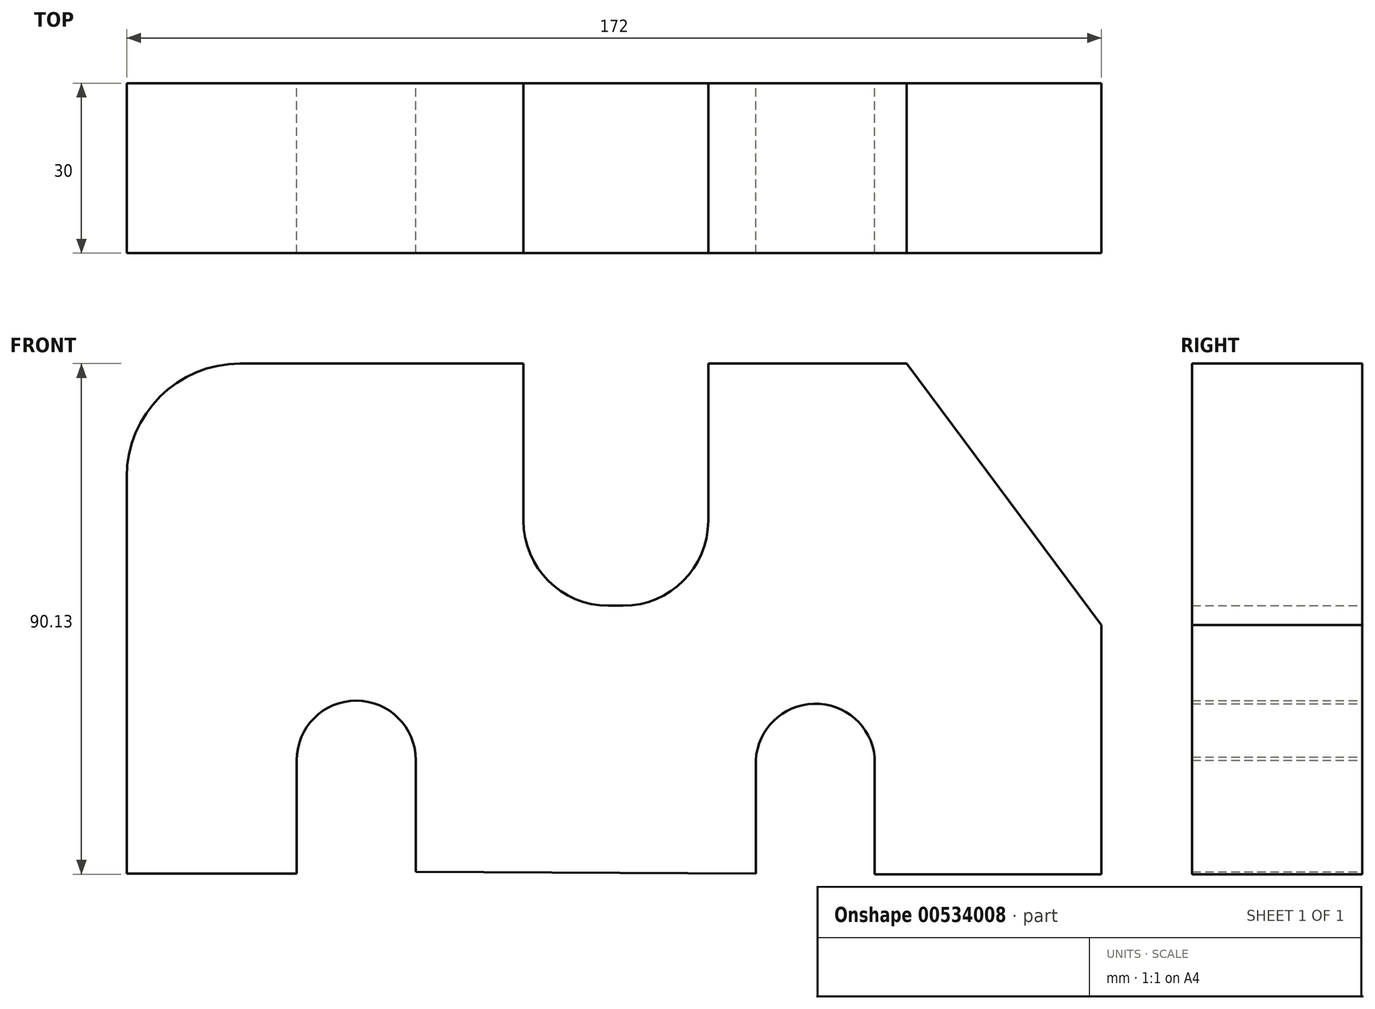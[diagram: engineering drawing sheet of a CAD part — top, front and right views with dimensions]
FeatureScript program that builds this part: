
annotation { "Feature Type Name" : "Feature", "Feature Type Description" : "" }
export const myFeature = defineFeature(function(context is Context, id is Id, definition is map)
    precondition{}
    {
        {
            var Q0;
            Q0=qCreatedBy(makeId("Front.planeOp"),FACE);
            var sketch = newSketch(context, id + "F0", { "sketchPlane" : qUnion([Q0])});
            skLineSegment(sketch, "E0", {"start": v(-52.5, -20.13) * mm, "end": v(-52.5, -40.13) * mm});
            skLineSegment(sketch, "E1", {"start": v(-52.5, -40.13) * mm, "end": v(-82.5, -40.13) * mm});
            skLineSegment(sketch, "E2", {"start": v(-82.5, -40.13) * mm, "end": v(-82.5, 29.87) * mm});
            skLineSegment(sketch, "E3", {"start": v(-62.5, 49.87) * mm, "end": v(-12.5, 49.87) * mm});
            skLineSegment(sketch, "E4", {"start": v(-12.5, 49.87) * mm, "end": v(-12.5, 22.12) * mm});
            skLineSegment(sketch, "E5", {"start": v(2.5, 7.12) * mm, "end": v(5.1, 7.12) * mm});
            skLineSegment(sketch, "E6", {"start": v(20.1, 22.12) * mm, "end": v(20.1, 49.87) * mm});
            skPoint(sketch, "E7.visualSharp", {"position": v(-82.5, 49.87) * mm});
            skArc(sketch, "E7.filletArc", {"start": v(-62.5, 49.87) * mm, "mid": v(-76.64, 44.02) * mm, "end": v(-82.5, 29.87) * mm});
            skPoint(sketch, "E8.start.orphan", {"position": v(64.04, -10.18) * mm});
            skLineSegment(sketch, "E9", {"start": v(28.5, -20.13) * mm, "end": v(28.5, -40.13) * mm});
            skPoint(sketch, "E10.start.orphan", {"position": v(-31.5, -10.18) * mm});
            skLineSegment(sketch, "E11", {"start": v(-42.5, -10.13) * mm, "end": v(-41.5, -10.13) * mm});
            skLineSegment(sketch, "E12", {"start": v(-31.5, -20.13) * mm, "end": v(-31.5, -39.81) * mm});
            skLineSegment(sketch, "E13", {"start": v(-31.5, -39.81) * mm, "end": v(28.5, -40.13) * mm});
            skPoint(sketch, "E14.visualSharp", {"position": v(-52.5, -10.13) * mm});
            skPoint(sketch, "E15.visualSharp", {"position": v(-31.5, -10.13) * mm});
            skPoint(sketch, "E16.visualSharp", {"position": v(28.5, -10.18) * mm});
            skPoint(sketch, "E17.end.orphan", {"position": v(65.03, -40.13) * mm});
            skPoint(sketch, "E18.visualSharp", {"position": v(-12.5, 7.12) * mm});
            skArc(sketch, "E18.filletArc", {"start": v(-12.5, 22.12) * mm, "mid": v(-8.1, 11.52) * mm, "end": v(2.5, 7.12) * mm});
            skPoint(sketch, "E19.visualSharp", {"position": v(20.1, 7.12) * mm});
            skArc(sketch, "E19.filletArc", {"start": v(5.1, 7.12) * mm, "mid": v(15.71, 11.52) * mm, "end": v(20.1, 22.12) * mm});
            skLineSegment(sketch, "E20", {"start": v(49.5, -40.26) * mm, "end": v(89.5, -40.26) * mm});
            skLineSegment(sketch, "E21", {"start": v(89.5, -40.26) * mm, "end": v(89.5, 3.74) * mm});
            skLineSegment(sketch, "E22", {"start": v(49.5, -40.26) * mm, "end": v(49.5, -19.57) * mm});
            skPoint(sketch, "E23.start.orphan", {"position": v(49.5, -10.18) * mm});
            skLineSegment(sketch, "E24", {"start": v(20.1, 49.87) * mm, "end": v(55.1, 49.87) * mm});
            skLineSegment(sketch, "E25", {"start": v(55.1, 49.87) * mm, "end": v(89.5, 3.74) * mm});
            skPoint(sketch, "E26.start.orphan", {"position": v(39.5, -10.18) * mm});
            skArc(sketch, "E27", {"start": v(49.5, -19.57) * mm, "mid": v(38.75, -10.17) * mm, "end": v(28.5, -20.13) * mm});
            skArc(sketch, "E28", {"start": v(-31.5, -20.13) * mm, "mid": v(-42, -9.63) * mm, "end": v(-52.5, -20.13) * mm});
            skSolve(sketch);
        }
        {
            var Q0;
            Q0=makeQuery(id+"F0.imprint","IMPRINT",FACE,{"disambiguationData":[TD([[makeQuery(id+"F0.imprint","IMPRINT",EDGE,{"derivedFrom":sQuery(id+"F0.wireOp",EDGE,"E0")}),-1.0]])]});
            extrude(context, id + "F1", {"entities" : qUnion([Q0]), "depth" : 30 * mm, "offsetDistance" : 25 * mm});
        }
    });
